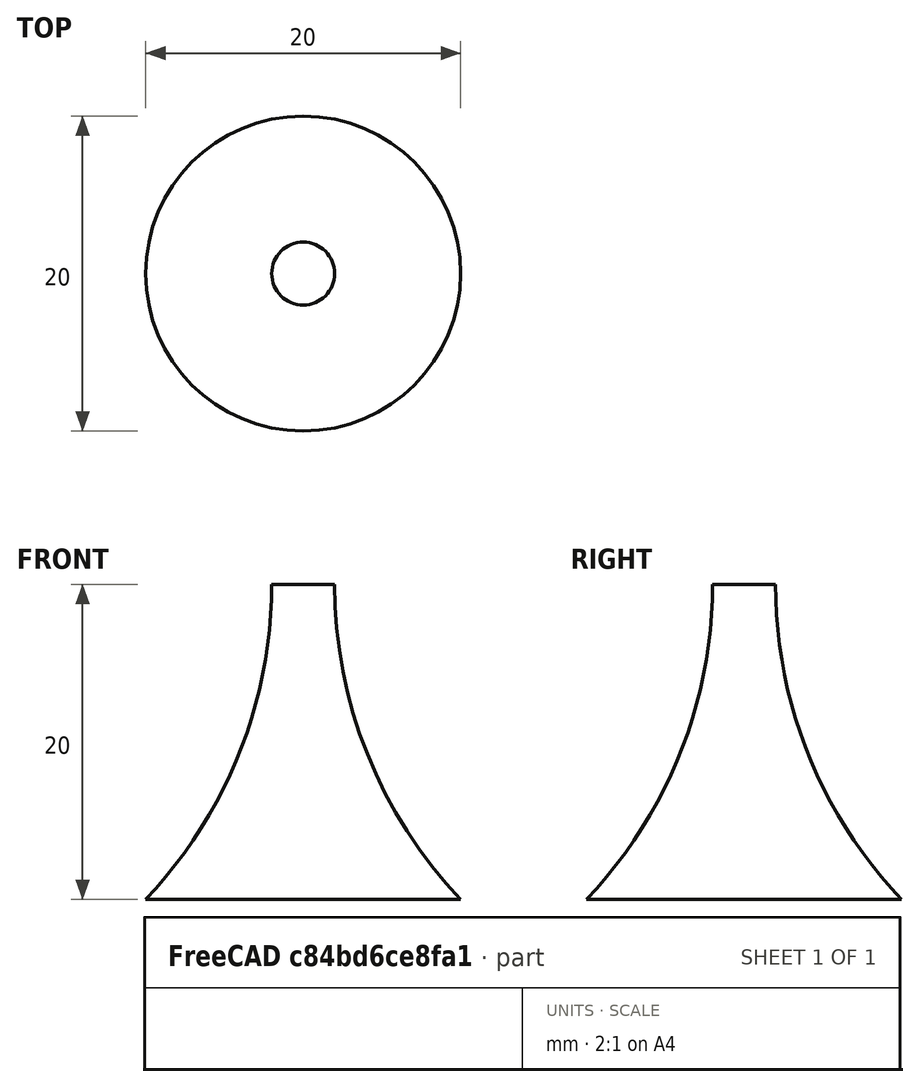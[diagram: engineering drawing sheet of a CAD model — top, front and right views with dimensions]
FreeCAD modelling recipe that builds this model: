
FCSTD DOCUMENT  (FreeCAD 0.22R35451 (Git))
Label: cone
License: All rights reserved
LicenseURL: http://en.wikipedia.org/wiki/All_rights_reserved
objects: Sketcher::SketchObject×1, PartDesign::Revolution×1, PartDesign::Body×1, App::Part×1
note: 4 computed .brp shape members not serialized (recipe doc carries the construction recipe); baked Part::Feature solids carry a one-line shape summary decoded from their .brp

FEATURE [Sketcher::SketchObject] Sketch
  FullyConstrained = true
  MapMode = 5
  Placement = pos=(0,0,0) rot=(1,0,0;1.5708rad)
  Support = -> [XZ_Plane001]
  sketch-geometry (4):
    g0: LineSegment StartX=0 StartY=0 StartZ=0 EndX=0 EndY=20 EndZ=0
    g1: LineSegment StartX=0 StartY=20 StartZ=0 EndX=2 EndY=20 EndZ=0
    g2: ArcOfCircle CenterX=31 CenterY=20 CenterZ=0 NormalX=0 NormalY=0 NormalZ=1 AngleXU=0 Radius=29 StartAngle=3.14159 EndAngle=3.90261
    g3: LineSegment StartX=10 StartY=0 StartZ=0 EndX=0 EndY=0 EndZ=0
  constraints (11):
    c: Coincident(g-1,g0)
    c: PointOnObject(g0,g-2)
    c: Coincident(g0,g1)
    c: Horizontal(g1)
    c: Perpendicular(g1,g2) = 4.71239
    c: PointOnObject(g2,g-1)
    c: Coincident(g2,g3)
    c: Coincident(g3,g0)
    c: DistanceX(g1,g1) = 2
    c: DistanceX(g3,g3) = 10
    c: DistanceY(g0,g0) = 20
FEATURE [PartDesign::Revolution] Revolution
  Angle = 360
  Angle2 = 60
  Axis = (0,2e-16,1)
  Base = (0,0,0)
  Placement = pos=(0,0,0) rot=(1,0,0;1.5708rad)
  Profile = -> Sketch
  ReferenceAxis = -> Sketch [V_Axis]
  Refine = true
  Reversed = true
  Type = 0
FEATURE [PartDesign::Body] Body  label="cone0"
  Group = -> [Sketch,Revolution]
  Origin = -> Origin001
  Tip = -> Revolution
FEATURE [App::Part] Part  label="cone"
  Group = -> [Body]
  Origin = -> Origin
